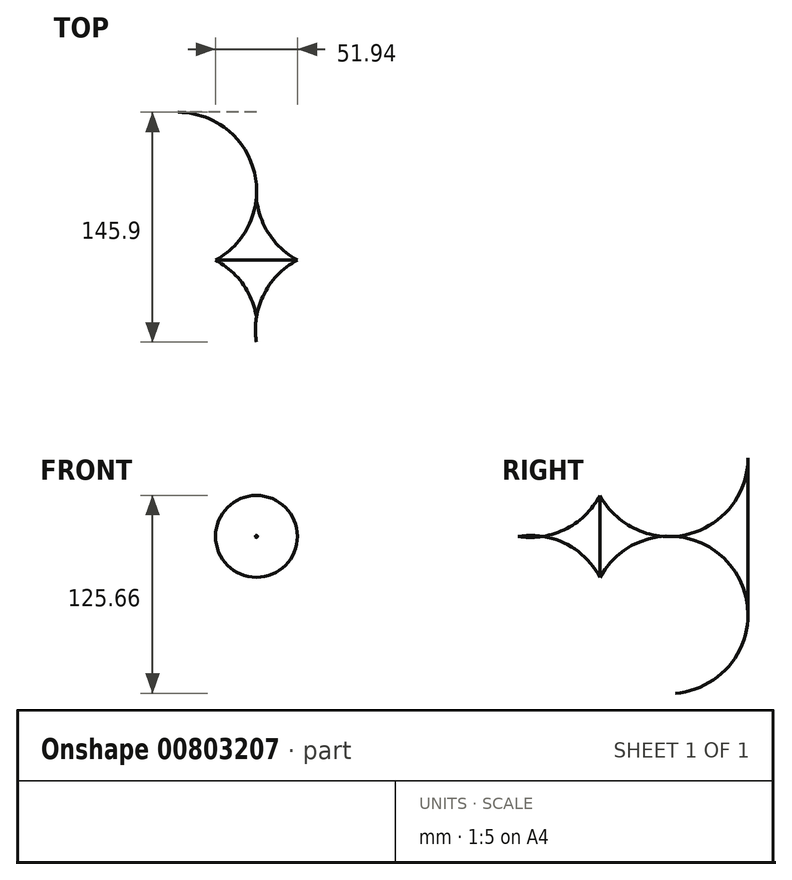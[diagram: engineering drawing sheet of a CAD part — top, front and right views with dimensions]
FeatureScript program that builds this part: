
annotation { "Feature Type Name" : "Feature", "Feature Type Description" : "" }
export const myFeature = defineFeature(function(context is Context, id is Id, definition is map)
    precondition{}
    {
        {
            var Q0;
            Q0=qCreatedBy(makeId("Top.planeOp"),FACE);
            var sketch = newSketch(context, id + "F0", { "sketchPlane" : qUnion([Q0])});
            skLineSegment(sketch, "E0", {"start": v(0, 0) * mm, "end": v(0, 80) * mm, "construction": true});
            skLineSegment(sketch, "E1", {"start": v(0, 0) * mm, "end": v(0, -88.33) * mm, "construction": true});
            skArc(sketch, "E2", {"start": v(25.97, 0) * mm, "mid": v(8.7, -15.13) * mm, "end": v(0, -36.38) * mm});
            skArc(sketch, "E3", {"start": v(0, 40) * mm, "mid": v(7.91, 16.7) * mm, "end": v(25.97, 0) * mm});
            skLineSegment(sketch, "E4", {"start": v(0, 40) * mm, "end": v(0, -36.38) * mm});
            skSolve(sketch);
        }
        {
            var Q0;
            Q0=makeQuery(id+"F0.imprint","IMPRINT",FACE,{"disambiguationData":[TD([[makeQuery(id+"F0.imprint","IMPRINT",EDGE,{"derivedFrom":sQuery(id+"F0.wireOp",EDGE,"E2")}),-1.0]])]});
            var Q1;
            Q1=sQuery(id+"F0.wireOp",EDGE,"E0");
            revolve(context, id + "F1", {"surfaceOperationType" : NewSurfaceOperationType.NEW, "entities" : qUnion([Q0]), "axis" : qUnion([Q1]), "revolveType" : RevolveType.FULL});
        }
    });
